annotation { "Feature Type Name" : "Feature", "Feature Type Description" : "" }
export const myFeature = defineFeature(function(context is Context, id is Id, definition is map)
    precondition{}
    {
        {
            var Q0;
            Q0=qCreatedBy(makeId("Front.planeOp"),FACE);
            var sketch = newSketch(context, id + "F0", { "sketchPlane" : qUnion([Q0])});
            skLineSegment(sketch, "E0", {"start": v(-70.37, 58.76) * mm, "end": v(-22.75, -63.08) * mm});
            skLineSegment(sketch, "E1", {"start": v(-70.37, 58.76) * mm, "end": v(-64.73, 60.97) * mm});
            skLineSegment(sketch, "E2", {"start": v(-64.73, 60.97) * mm, "end": v(-17.56, -59.73) * mm});
            skLineSegment(sketch, "E3", {"start": v(-17.56, -59.73) * mm, "end": v(-22.75, -63.08) * mm});
            skLineSegment(sketch, "E4", {"start": v(-17.56, -59.73) * mm, "end": v(0, 56.64) * mm});
            skLineSegment(sketch, "E5", {"start": v(-22.3, -47.6) * mm, "end": v(-6.57, 56.64) * mm});
            skLineSegment(sketch, "E6", {"start": v(-4.82, 56.64) * mm, "end": v(-6.57, 56.64) * mm});
            skLineSegment(sketch, "E7", {"start": v(-4.82, 56.64) * mm, "end": v(0, 56.64) * mm});
            skLineSegment(sketch, "E8", {"start": v(-0.21, 55.25) * mm, "end": v(26.02, -59.73) * mm});
            skLineSegment(sketch, "E9", {"start": v(26.02, -59.73) * mm, "end": v(34.89, -59.73) * mm});
            skLineSegment(sketch, "E10", {"start": v(-0.21, 55.25) * mm, "end": v(9.33, 57.43) * mm});
            skLineSegment(sketch, "E11", {"start": v(9.47, 56.83) * mm, "end": v(34.89, -59.73) * mm});
            skLineSegment(sketch, "E12", {"start": v(34.89, -59.73) * mm, "end": v(59.97, 53.32) * mm});
            skLineSegment(sketch, "E13", {"start": v(59.97, 53.32) * mm, "end": v(64.35, 52.35) * mm});
            skLineSegment(sketch, "E14", {"start": v(64.38, 50.2) * mm, "end": v(43.27, -59.73) * mm});
            skLineSegment(sketch, "E15", {"start": v(43.27, -59.73) * mm, "end": v(34.89, -59.73) * mm});
            skLineSegment(sketch, "E16", {"start": v(64.35, 52.35) * mm, "end": v(63.79, 47.12) * mm});
            skLineSegment(sketch, "E17", {"start": v(9.33, 57.43) * mm, "end": v(9.47, 56.83) * mm});
            skSolve(sketch);
        }
        {
            var Q0;
            Q0=makeQuery(id+"F0.imprint","IMPRINT",FACE,{"disambiguationData":[TD([[makeQuery(id+"F0.imprint","IMPRINT",EDGE,{"derivedFrom":sQuery(id+"F0.wireOp",EDGE,"E0")}),1.0]])]});
            var Q1;
            {var subQ0=sQuery(id+"F0.wireOp",EDGE,"E5");Q1=makeQuery(id+"F0.imprint","IMPRINT",FACE,{"disambiguationData":[TD([[makeQuery(id+"F0.imprint","IMPRINT",EDGE,{"derivedFrom":subQ0}),-1.0]])]});}
            var Q2;
            Q2=makeQuery(id+"F0.imprint","IMPRINT",FACE,{"disambiguationData":[TD([[makeQuery(id+"F0.imprint","IMPRINT",EDGE,{"derivedFrom":sQuery(id+"F0.wireOp",EDGE,"E8")}),1.0]])]});
            var Q3;
            Q3=makeQuery(id+"F0.imprint","IMPRINT",FACE,{"disambiguationData":[TD([[makeQuery(id+"F0.imprint","IMPRINT",EDGE,{"derivedFrom":sQuery(id+"F0.wireOp",EDGE,"E12")}),-1.0]])]});
            extrude(context, id + "F1", {"entities" : qUnion([Q0, Q1, Q2, Q3]), "depth" : 119.38 * mm});
        }
        {
            var Q0;
            Q0=makeQuery(id+"F1.opExtrude","CAP_FACE",FACE,{"disambiguationData":[OSD([sQuery(id+"F0.wireOp",EDGE,"E0"),sQuery(id+"F0.wireOp",EDGE,"E1"),sQuery(id+"F0.wireOp",EDGE,"E2"),sQuery(id+"F0.wireOp",EDGE,"E3"),sQuery(id+"F0.wireOp",EDGE,"E4"),sQuery(id+"F0.wireOp",EDGE,"E5"),sQuery(id+"F0.wireOp",EDGE,"E6"),sQuery(id+"F0.wireOp",EDGE,"E7")])],"isStart":false});
            var Q1;
            Q1=makeQuery(id+"F1.opExtrude","CAP_FACE",FACE,{"disambiguationData":[OSD([sQuery(id+"F0.wireOp",EDGE,"E8"),sQuery(id+"F0.wireOp",EDGE,"E9"),sQuery(id+"F0.wireOp",EDGE,"E10"),sQuery(id+"F0.wireOp",EDGE,"E11"),sQuery(id+"F0.wireOp",EDGE,"E17")])],"isStart":false});
            var Q2;
            Q2=makeQuery(id+"F1.opExtrude","CAP_FACE",FACE,{"disambiguationData":[OSD([sQuery(id+"F0.wireOp",EDGE,"E12"),sQuery(id+"F0.wireOp",EDGE,"E13"),sQuery(id+"F0.wireOp",EDGE,"E14"),sQuery(id+"F0.wireOp",EDGE,"E15"),sQuery(id+"F0.wireOp",EDGE,"E16")])],"isStart":false});
            extrude(context, id + "F2", {"entities" : qUnion([Q0, Q1, Q2]), "depth" : 406425.4 * mm});
        }
    });